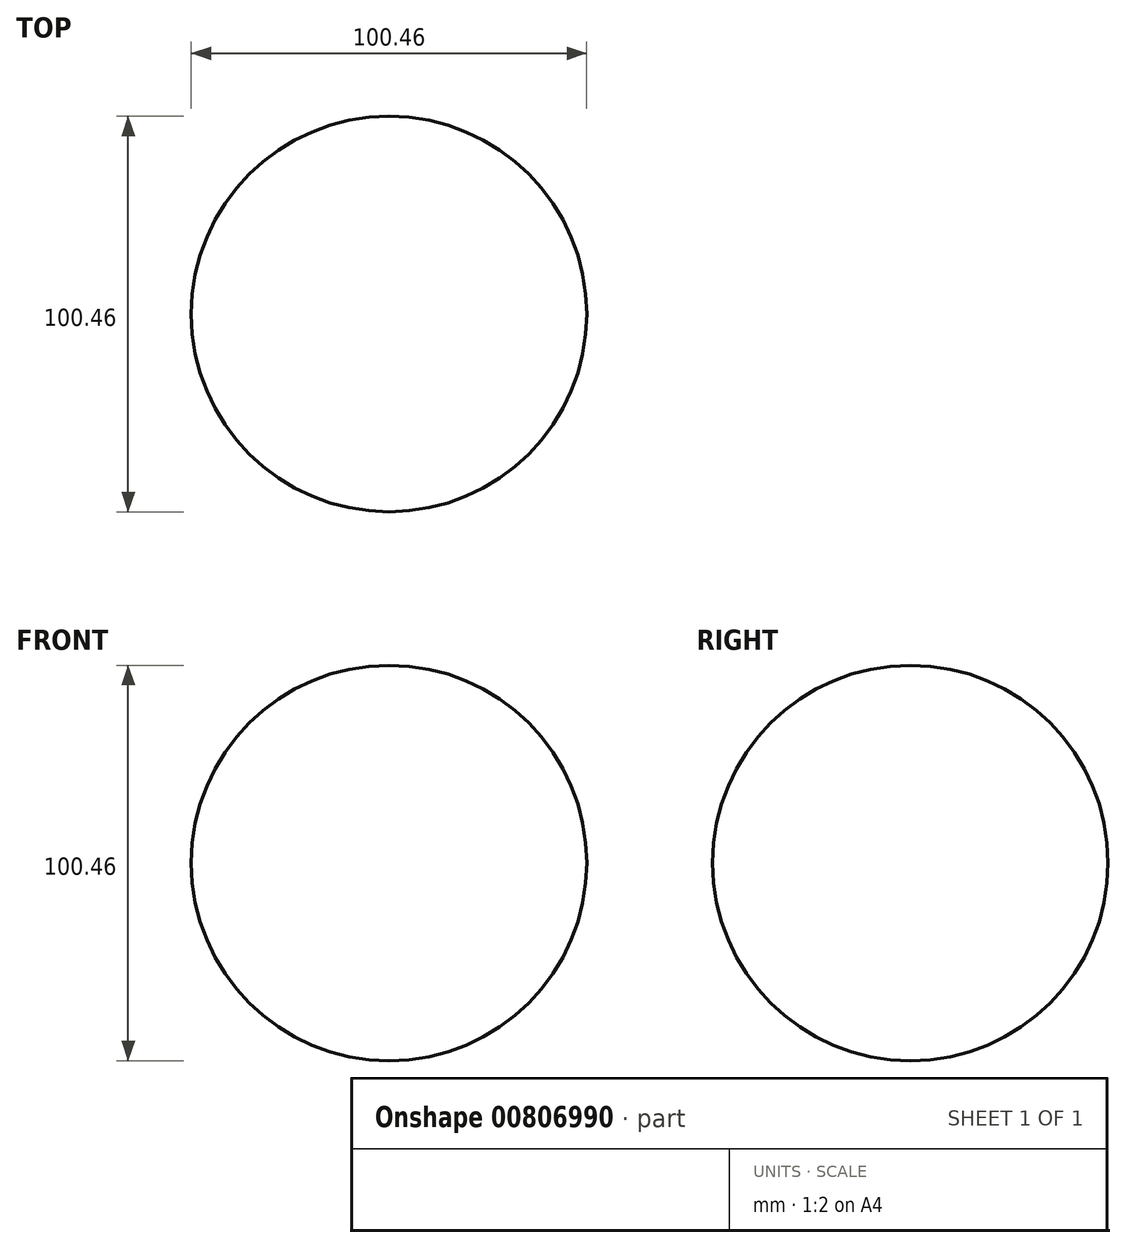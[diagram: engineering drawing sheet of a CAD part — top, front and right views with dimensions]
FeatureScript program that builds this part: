
annotation { "Feature Type Name" : "Feature", "Feature Type Description" : "" }
export const myFeature = defineFeature(function(context is Context, id is Id, definition is map)
    precondition{}
    {
        {
            var Q0;
            Q0=qCreatedBy(makeId("Front.planeOp"),FACE);
            var sketch = newSketch(context, id + "F0", { "sketchPlane" : qUnion([Q0])});
            skCircle(sketch, "E0", {"center": v(0, 0) * mm, "radius": 50.23 * mm});
            skLineSegment(sketch, "E1", {"start": v(0, -56.2) * mm, "end": v(0, 57.29) * mm});
            skSolve(sketch);
        }
        {
            var Q0;
            {var subQ0=sQuery(id+"F0.wireOp",EDGE,"E1");var subQ1=sQuery(id+"F0.wireOp",EDGE,"E0");var subQ2=makeQuery(id+"F0.imprint","INTERSECT",VERTEX,{"disambiguationData":[OD(0.0)],"derivedFrom":[subQ1,subQ0]});Q0=makeQuery(id+"F0.imprint","IMPRINT",FACE,{"disambiguationData":[TD([[makeQuery(id+"F0.imprint","IMPRINT",EDGE,{"disambiguationData":[TD([[subQ2,-1.0]])],"derivedFrom":subQ1}),1.0]])]});}
            var Q1;
            Q1=sQuery(id+"F0.wireOp",EDGE,"E1");
            revolve(context, id + "F1", {"surfaceOperationType" : NewSurfaceOperationType.NEW, "entities" : qUnion([Q0]), "axis" : qUnion([Q1]), "revolveType" : RevolveType.FULL});
        }
    });
